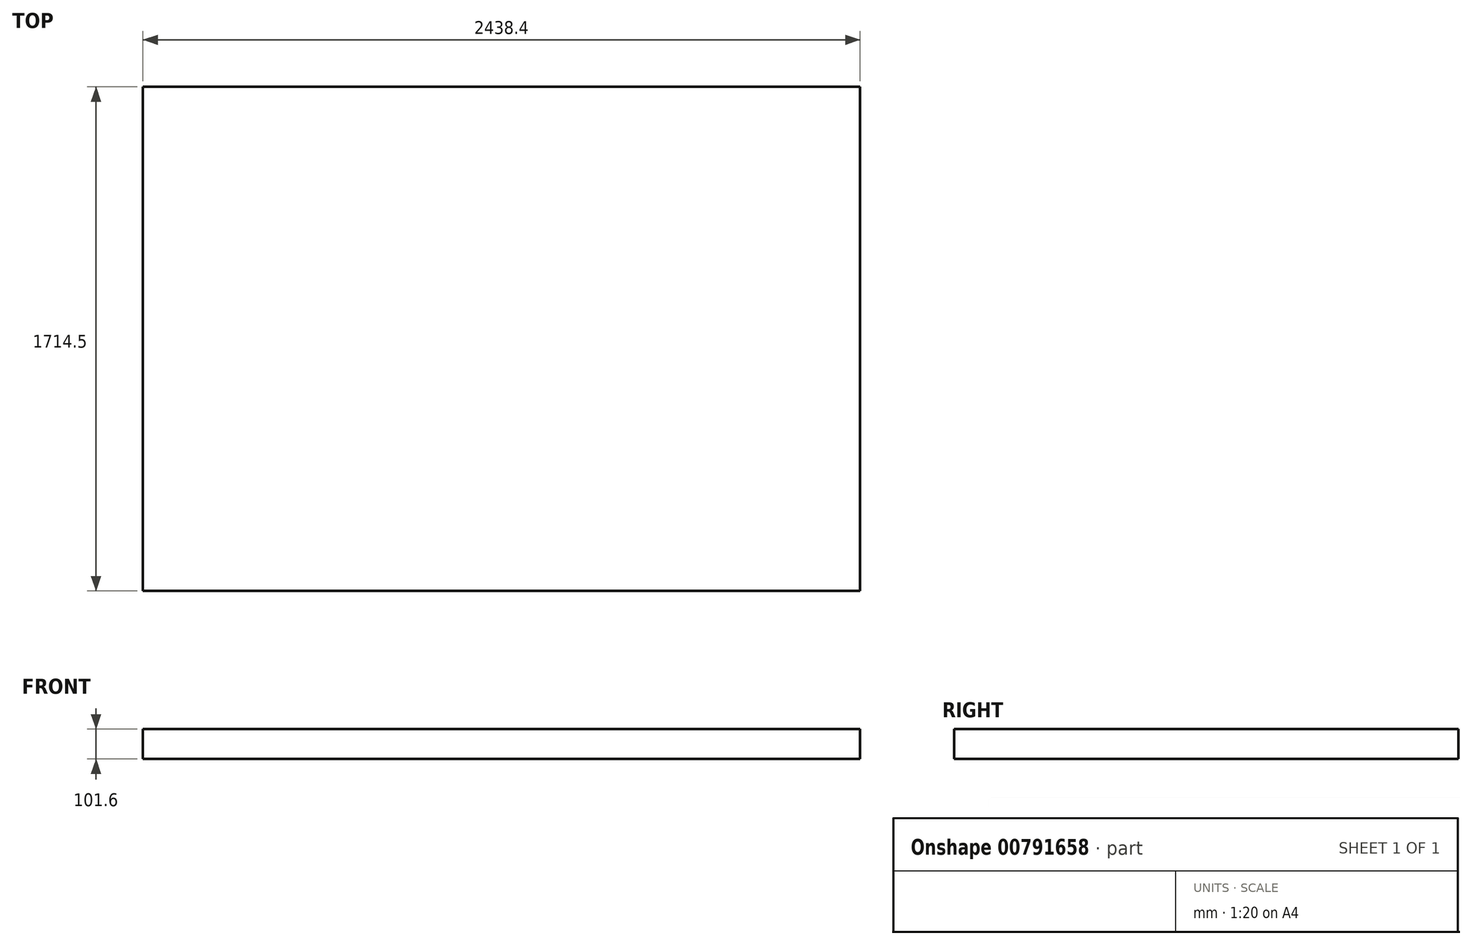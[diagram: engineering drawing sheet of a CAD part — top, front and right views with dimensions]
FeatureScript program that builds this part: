
annotation { "Feature Type Name" : "Feature", "Feature Type Description" : "" }
export const myFeature = defineFeature(function(context is Context, id is Id, definition is map)
    precondition{}
    {
        {
            var Q0;
            Q0=qCreatedBy(makeId("Top.planeOp"),FACE);
            var sketch = newSketch(context, id + "F0", { "sketchPlane" : qUnion([Q0])});
            skLineSegment(sketch, "E0.bottom", {"start": v(1219.2, -857.25) * mm, "end": v(-1219.2, -857.25) * mm});
            skLineSegment(sketch, "E0.top", {"start": v(1219.2, 857.25) * mm, "end": v(-1219.2, 857.25) * mm});
            skLineSegment(sketch, "E0.left", {"start": v(1219.2, -857.25) * mm, "end": v(1219.2, 857.25) * mm});
            skLineSegment(sketch, "E0.right", {"start": v(-1219.2, -857.25) * mm, "end": v(-1219.2, 857.25) * mm});
            skPoint(sketch, "E0.middle", {"position": v(0, 0) * mm});
            skSolve(sketch);
        }
        {
            var Q0;
            Q0 = qSketchRegion(id + "F0", true);
            extrude(context, id + "F1", {"entities" : qUnion([Q0]), "oppositeDirection" : true, "depth" : 101.6 * mm, "offsetDistance" : 25.4 * mm});
        }
    });
